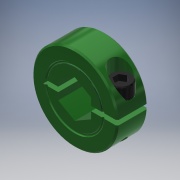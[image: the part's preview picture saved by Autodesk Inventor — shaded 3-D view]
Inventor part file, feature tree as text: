
AUTODESK INVENTOR PART (.ipt)
format: ipt  version: 2017.1 (Build 211199000, 199)  size: 312,320 bytes
history: native  units: in
note: dims shown in document units (in); Inventor stores cm internally (conversion verified against a paired STEP export)
features: extrude x2, sketch x2, other x1, imported_body x1
ambient origin geometry x8: Origin, YZ Plane, XZ Plane, XY Plane, X Axis, Y Axis, Z Axis, Center Point
bodies: Solid1 (feature_tree)
feature tree (6):
  other  "CL-8-A1"
  extrude  "Extrusion1"  Depth=0.4375in TaperAngle=0.0deg
  extrude  "Extrusion2"  [1 undecoded]
  imported_body  "Base1"
  sketch  "Sketch2"  dims[d0=0.5in d1=0.4375in d2=0.0in]
  sketch  "Sketch3"  dims[d3=1.0in d4=0.0in]
note: 1 required parameter value undecoded (feature->parameter linkage not recoverable at this tier; creation-order binding heuristic only, values carry confidence <= 0.55)
